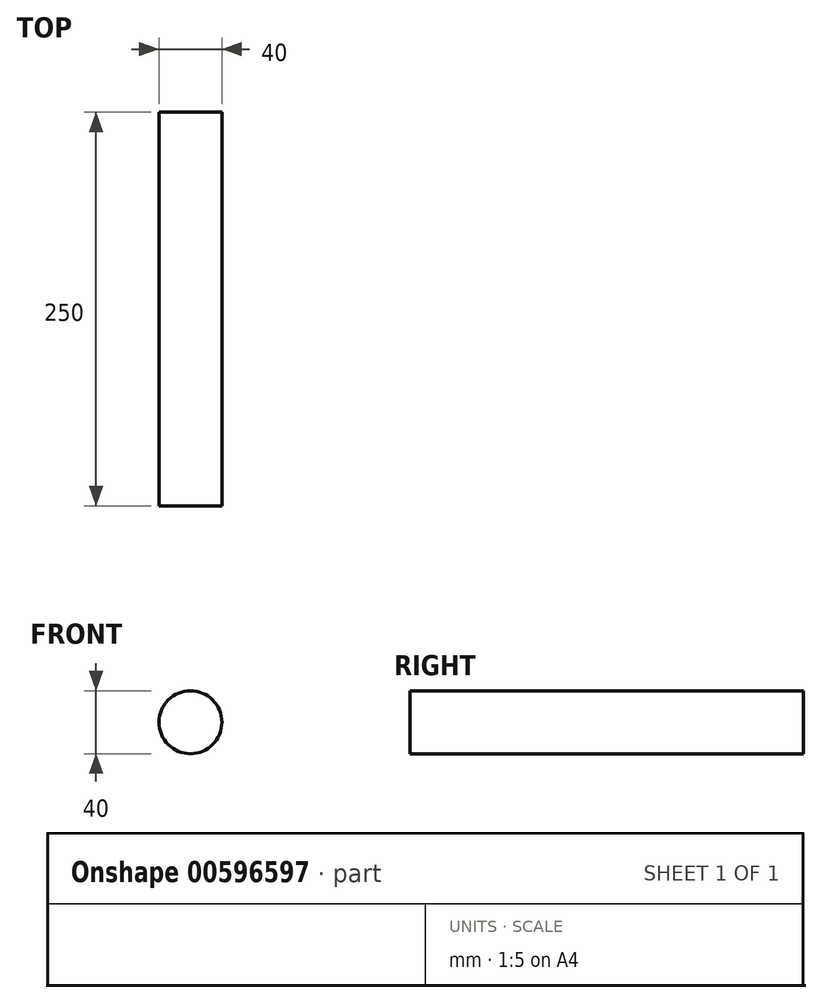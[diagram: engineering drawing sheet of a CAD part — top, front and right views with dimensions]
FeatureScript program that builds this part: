
annotation { "Feature Type Name" : "Feature", "Feature Type Description" : "" }
export const myFeature = defineFeature(function(context is Context, id is Id, definition is map)
    precondition{}
    {
        {
            var Q0;
            Q0=qCreatedBy(makeId("Front.planeOp"),FACE);
            var sketch = newSketch(context, id + "F0", { "sketchPlane" : qUnion([Q0])});
            skCircle(sketch, "E0", {"center": v(0, 0) * mm, "radius": 20 * mm});
            skSolve(sketch);
        }
        {
            var Q0;
            Q0=makeQuery(id+"F0.imprint","IMPRINT",FACE,{"disambiguationData":[TD([[makeQuery(id+"F0.imprint","IMPRINT",EDGE,{"derivedFrom":sQuery(id+"F0.wireOp",EDGE,"E0")}),1.0]])]});
            extrude(context, id + "F1", {"entities" : qUnion([Q0]), "depth" : 250 * mm, "offsetDistance" : 25 * mm});
        }
    });
